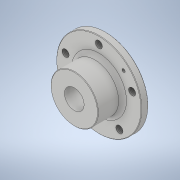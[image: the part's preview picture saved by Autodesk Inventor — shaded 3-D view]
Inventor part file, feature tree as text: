
AUTODESK INVENTOR PART (.ipt)
format: ipt  version: 2021 (Build 250183000, 183)  size: 195,584 bytes
history: native  units: in
note: dims shown in document units (in); Inventor stores cm internally (conversion verified against a paired STEP export)
features: thread x6, sketch x5, extrude x4, fillet x2, revolve x1, chamfer x1
ambient origin geometry x8: Origin, YZ Plane, XZ Plane, XY Plane, X Axis, Y Axis, Z Axis, Center Point
bodies: Solid1 (feature_tree)
feature tree (19):
  revolve  "Revolution1"  [1 undecoded]
  extrude  "Extrusion1"  Depth=0.435in
  extrude  "Extrusion2"  Depth=0.2in
  fillet  "Fillet1"  Radius=0.16in
  chamfer  "Chamfer1"  Distance=2.0in
  fillet  "Fillet2"  Radius=1.0in
  extrude  "Extrusion3"  Depth=0.435in
  thread  "Thread1"  [1 undecoded]
  thread  "Thread2"  [1 undecoded]
  thread  "Thread3"  [1 undecoded]
  thread  "Thread4"  [1 undecoded]
  thread  "Thread5"  [1 undecoded]
  thread  "Thread6"  [1 undecoded]
  extrude  "Extrusion4"  Depth=0.435in TaperAngle=360.0deg
  sketch  "Sketch1"  dims[d0=1.5in d1=1.56in]
  sketch  "Sketch2"  dims[d2=1.2in d3=0.435in]
  sketch  "Sketch3"  dims[d4=1.42in d5=0.2in d6=0.16in]
  sketch  "Sketch4"  dims[d7=0.52in]
  sketch  "Sketch5"  dims[d8=90.0deg d9=2.0in d10=1.0in d11=0.0in d12=1.25in d13=1.0in d14=0.0in d15=0.075in d16=0.03in d17=0.125in d18=45.0deg d19=0.25in d20=0.452in d21=0.48in d22=1.9685in d24=360.0deg d26=45.0deg d27=0.2in d28=0.2in d29=0.0in d30=0.435in d31=0.0in d32=0.435in d33=0.0in d34=0.435in d35=0.0in d36=0.435in d37=0.0in d38=0.435in d39=0.0in d40=0.435in d41=0.0in d42=1.0in d43=0.0in]
note: 7 required parameter values undecoded (feature->parameter linkage not recoverable at this tier; creation-order binding heuristic only, values carry confidence <= 0.55)